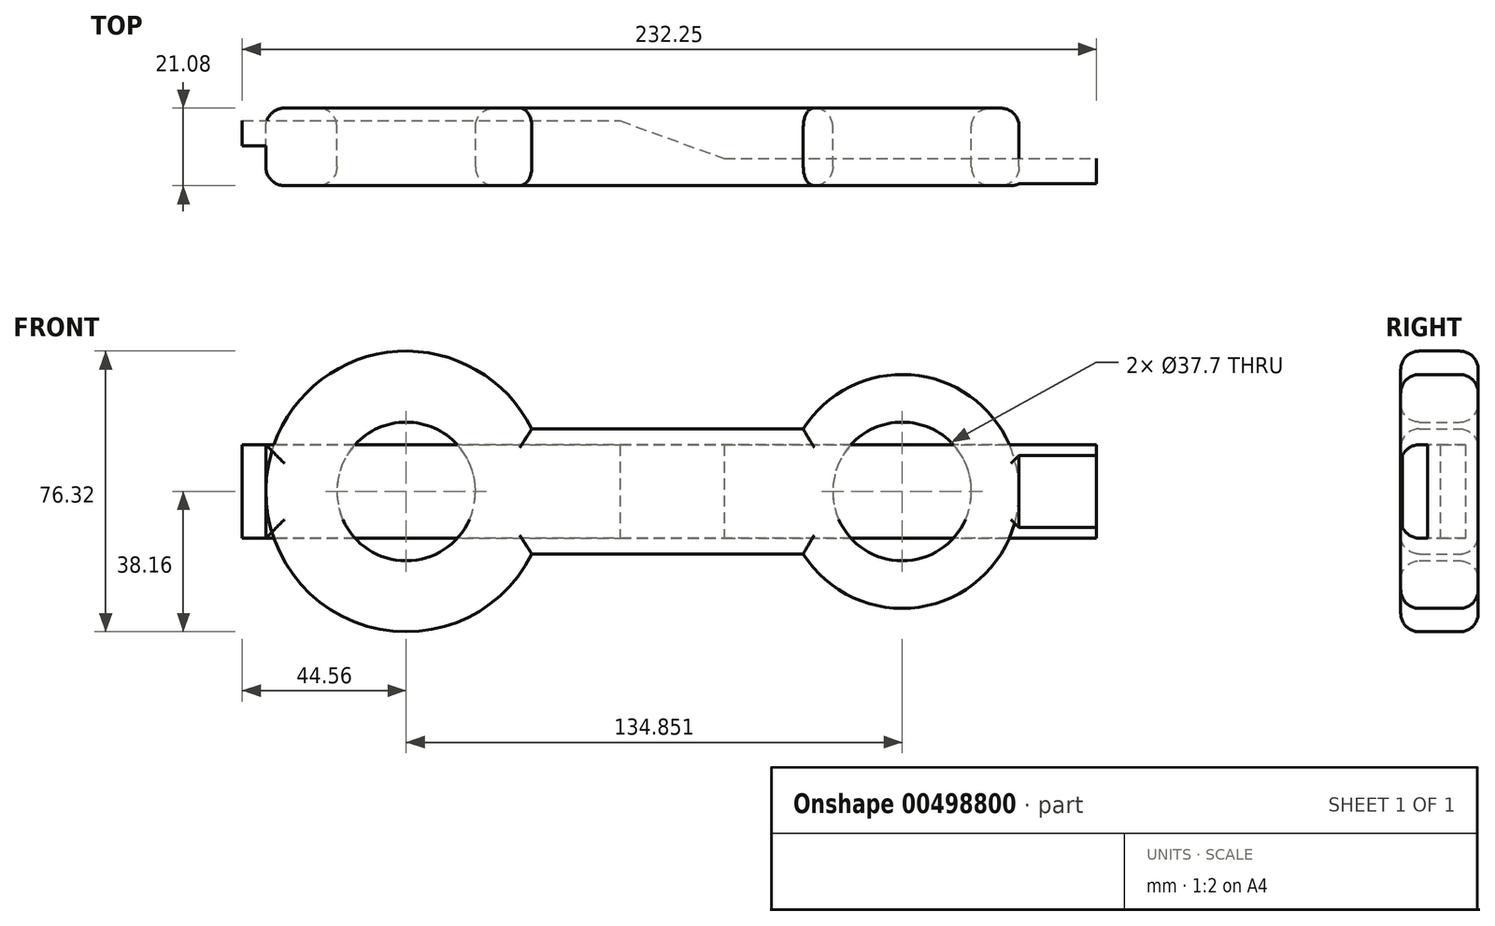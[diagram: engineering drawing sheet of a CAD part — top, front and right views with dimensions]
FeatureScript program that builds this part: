
annotation { "Feature Type Name" : "Feature", "Feature Type Description" : "" }
export const myFeature = defineFeature(function(context is Context, id is Id, definition is map)
    precondition{}
    {
        {
            var Q0;
            Q0=qCreatedBy(makeId("Front.planeOp"),FACE);
            var sketch = newSketch(context, id + "F0", { "sketchPlane" : qUnion([Q0])});
            skCircle(sketch, "E0", {"center": v(0, 0) * mm, "radius": 38.16 * mm});
            skCircle(sketch, "E1", {"center": v(134.85, 0) * mm, "radius": 31.8 * mm});
            skLineSegment(sketch, "E2", {"start": v(0, 0) * mm, "end": v(134.85, 0) * mm, "construction": true});
            skLineSegment(sketch, "E3", {"start": v(34.16, 17.02) * mm, "end": v(107.98, 17.02) * mm});
            skLineSegment(sketch, "E4", {"start": v(34.16, -17.02) * mm, "end": v(107.98, -17.02) * mm});
            skCircle(sketch, "E5", {"center": v(0, 0) * mm, "radius": 18.85 * mm});
            skCircle(sketch, "E6", {"center": v(134.85, 0) * mm, "radius": 18.85 * mm});
            skSolve(sketch);
        }
        {
            var Q0;
            Q0 = qSketchRegion(id + "F0", true);
            extrude(context, id + "F1", {"entities" : qUnion([Q0]), "depth" : 21.08 * mm});
        }
        {
            var Q0;
            Q0=qCreatedBy(makeId("Top.planeOp"),FACE);
            var sketch = newSketch(context, id + "F2", { "sketchPlane" : qUnion([Q0])});
            skLineSegment(sketch, "E7", {"start": v(-44.56, -10.32) * mm, "end": v(56.94, -10.32) * mm});
            skLineSegment(sketch, "E8", {"start": v(56.94, -10.32) * mm, "end": v(85.28, -20.59) * mm});
            skLineSegment(sketch, "E9", {"start": v(85.28, -20.59) * mm, "end": v(187.69, -20.59) * mm});
            skLineSegment(sketch, "E10.0", {"start": v(86.49, -13.73) * mm, "end": v(187.69, -13.73) * mm});
            skLineSegment(sketch, "E10.1", {"start": v(58.14, -3.47) * mm, "end": v(86.49, -13.73) * mm});
            skLineSegment(sketch, "E10.2", {"start": v(-44.56, -3.47) * mm, "end": v(58.14, -3.47) * mm});
            skLineSegment(sketch, "E11", {"start": v(-44.56, -10.32) * mm, "end": v(-44.56, -3.47) * mm});
            skLineSegment(sketch, "E12", {"start": v(187.69, -20.59) * mm, "end": v(187.69, -13.73) * mm});
            skLineSegment(sketch, "E13", {"start": v(-38.16, -21.08) * mm, "end": v(-38.16, 0) * mm});
            skLineSegment(sketch, "E14", {"start": v(166.65, 0) * mm, "end": v(166.65, -21.08) * mm});
            skLineSegment(sketch, "E15.0", {"start": v(34.16, -21.08) * mm, "end": v(107.98, -21.08) * mm});
            skLineSegment(sketch, "E16.0", {"start": v(34.16, 0) * mm, "end": v(107.98, 0) * mm});
            skLineSegment(sketch, "E17.0", {"start": v(34.16, -21.08) * mm, "end": v(-38.16, -21.08) * mm});
            skLineSegment(sketch, "E18.0", {"start": v(107.98, -21.08) * mm, "end": v(166.65, -21.08) * mm});
            skSolve(sketch);
        }
        {
            var Q0;
            Q0 = qSketchRegion(id + "F2", true);
            extrude(context, id + "F3", {"entities" : qUnion([Q0]), "endBound" : BoundingType.SYMMETRIC, "depth" : 25.4 * mm});
        }
        {
            var Q0;
            Q0=makeQuery(id+"F3.opExtrude","SWEPT_FACE",FACE,{"disambiguationData":[OSD([sQuery(id+"F2.wireOp",EDGE,"E15.0"),sQuery(id+"F2.wireOp",EDGE,"E17.0"),sQuery(id+"F2.wireOp",EDGE,"E18.0")])]});
            var Q1;
            Q1=makeQuery(id+"F1.opExtrude","CAP_FACE",FACE,{"disambiguationData":[OSD([sQuery(id+"F0.wireOp",EDGE,"E0"),sQuery(id+"F0.wireOp",EDGE,"E1"),sQuery(id+"F0.wireOp",EDGE,"E3"),sQuery(id+"F0.wireOp",EDGE,"E4"),sQuery(id+"F0.wireOp",EDGE,"E5"),sQuery(id+"F0.wireOp",EDGE,"E6")])],"isStart":false});
            var Q2;
            Q2=makeQuery(id+"F1.opExtrude","CAP_EDGE",EDGE,{"disambiguationData":[OSD([sQuery(id+"F0.wireOp",EDGE,"E5")])],"isStart":true});
            var Q3;
            Q3=makeQuery(id+"F1.opExtrude","CAP_FACE",FACE,{"disambiguationData":[OSD([sQuery(id+"F0.wireOp",EDGE,"E0"),sQuery(id+"F0.wireOp",EDGE,"E1"),sQuery(id+"F0.wireOp",EDGE,"E3"),sQuery(id+"F0.wireOp",EDGE,"E4"),sQuery(id+"F0.wireOp",EDGE,"E5"),sQuery(id+"F0.wireOp",EDGE,"E6")])],"isStart":true});
            fillet(context, id + "F4", {"entities" : qUnion([Q0, Q1, Q2, Q3]), "radius" : 5.08 * mm, "tangentPropagation" : true, "allowEdgeOverflow" : false});
        }
    });
